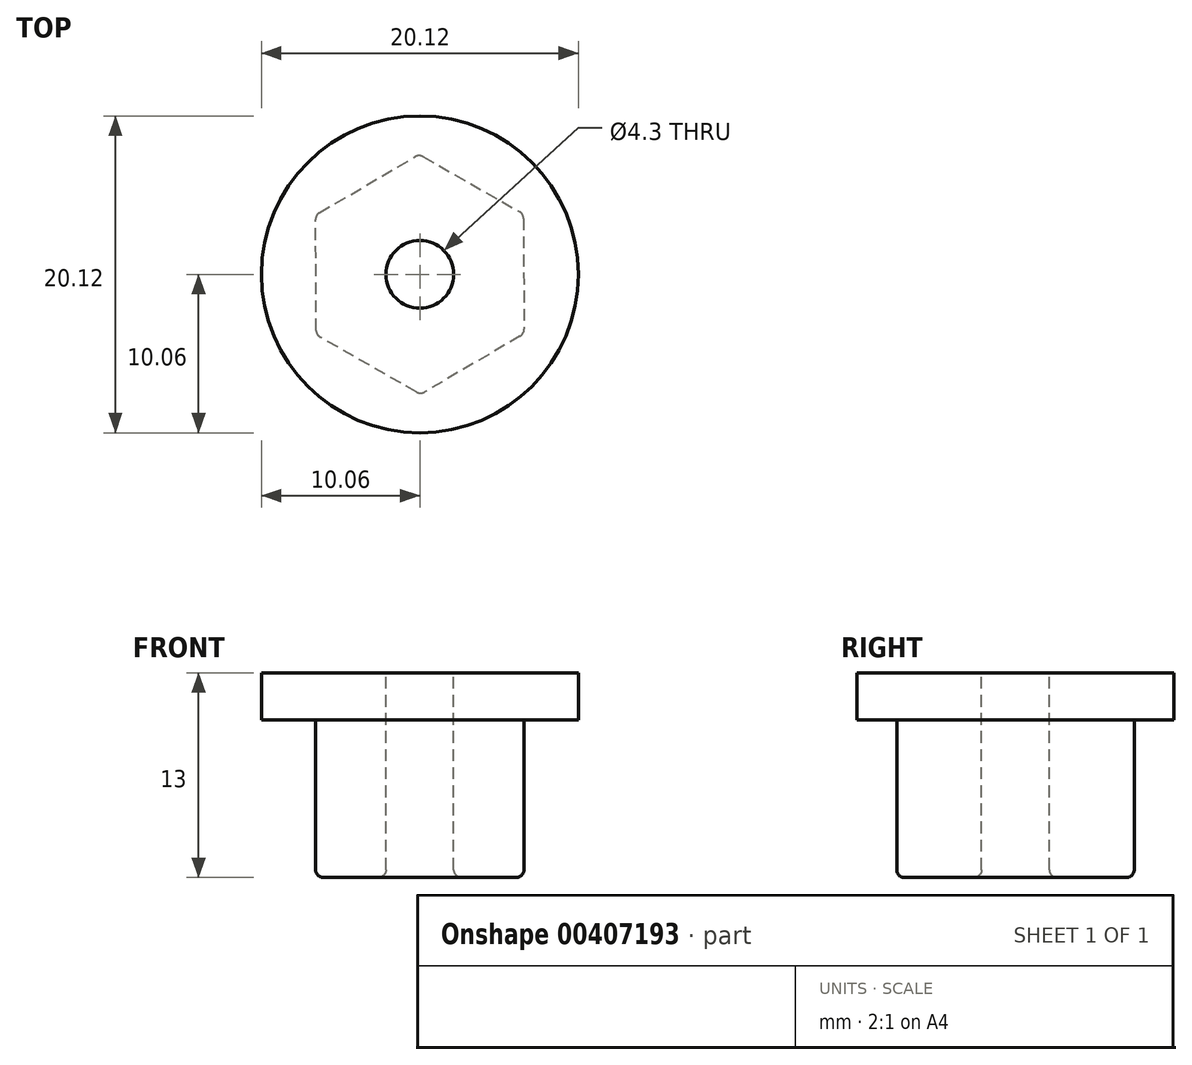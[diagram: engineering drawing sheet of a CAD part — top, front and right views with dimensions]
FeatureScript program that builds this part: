
annotation { "Feature Type Name" : "Feature", "Feature Type Description" : "" }
export const myFeature = defineFeature(function(context is Context, id is Id, definition is map)
    precondition{}
    {
        {
            var Q0;
            Q0=qCreatedBy(makeId("Top.planeOp"),FACE);
            var sketch = newSketch(context, id + "F0", { "sketchPlane" : qUnion([Q0])});
            skCircle(sketch, "E0.cCircle", {"center": v(0, 0) * mm, "radius": 6.6 * mm, "construction": true});
            skLineSegment(sketch, "E0.0", {"start": v(-0.04, 7.62) * mm, "end": v(6.58, 3.84) * mm});
            skLineSegment(sketch, "E0.1", {"start": v(6.58, 3.84) * mm, "end": v(6.62, -3.78) * mm});
            skLineSegment(sketch, "E0.2", {"start": v(6.62, -3.78) * mm, "end": v(0.04, -7.62) * mm});
            skLineSegment(sketch, "E0.3", {"start": v(0.04, -7.62) * mm, "end": v(-6.58, -3.84) * mm});
            skLineSegment(sketch, "E0.4", {"start": v(-6.58, -3.84) * mm, "end": v(-6.62, 3.78) * mm});
            skLineSegment(sketch, "E0.5", {"start": v(-6.62, 3.78) * mm, "end": v(-0.04, 7.62) * mm});
            skPoint(sketch, "E0.0.midPoint", {"position": v(3.27, 5.73) * mm});
            skSolve(sketch);
        }
        {
            var Q0;
            Q0 = qSketchRegion(id + "F0", true);
            extrude(context, id + "F1", {"entities" : qUnion([Q0]), "depth" : 10 * mm});
        }
        {
            var Q0;
            Q0=makeQuery(id+"F1.opExtrude","CAP_FACE",FACE,{"disambiguationData":[OSD([sQuery(id+"F0.wireOp",EDGE,"E0.0"),sQuery(id+"F0.wireOp",EDGE,"E0.1"),sQuery(id+"F0.wireOp",EDGE,"E0.2"),sQuery(id+"F0.wireOp",EDGE,"E0.3"),sQuery(id+"F0.wireOp",EDGE,"E0.4"),sQuery(id+"F0.wireOp",EDGE,"E0.5")])],"isStart":false});
            var sketch = newSketch(context, id + "F2", { "sketchPlane" : qUnion([Q0])});
            skCircle(sketch, "E1", {"center": v(0, 0) * mm, "radius": 10.06 * mm});
            skSolve(sketch);
        }
        {
            var Q0;
            Q0 = qSketchRegion(id + "F2", true);
            extrude(context, id + "F3", {"entities" : qUnion([Q0]), "operationType" : NewBodyOperationType.ADD, "depth" : 3 * mm});
        }
        {
            var Q0;
            Q0=makeQuery(id+"F3.opExtrude","CAP_FACE",FACE,{"disambiguationData":[OSD([sQuery(id+"F2.wireOp",EDGE,"E1")])],"isStart":false});
            var sketch = newSketch(context, id + "F4", { "sketchPlane" : qUnion([Q0])});
            skCircle(sketch, "E2", {"center": v(0, 0) * mm, "radius": 2.15 * mm});
            skSolve(sketch);
        }
        {
            var Q0;
            Q0 = qSketchRegion(id + "F4", true);
            extrude(context, id + "F5", {"entities" : qUnion([Q0]), "operationType" : NewBodyOperationType.REMOVE, "oppositeDirection" : true, "depth" : 25 * mm});
        }
        {
            var Q0;
            Q0=makeQuery(id+"F1.opExtrude","SWEPT_EDGE",EDGE,{"disambiguationData":[OSD([sQuery(id+"F0.wireOp",EDGE,"E0.0"),sQuery(id+"F0.wireOp",EDGE,"E0.5")])]});
            var Q1;
            Q1=makeQuery(id+"F1.opExtrude","SWEPT_EDGE",EDGE,{"disambiguationData":[OSD([sQuery(id+"F0.wireOp",EDGE,"E0.0"),sQuery(id+"F0.wireOp",EDGE,"E0.1")])]});
            var Q2;
            Q2=makeQuery(id+"F1.opExtrude","SWEPT_EDGE",EDGE,{"disambiguationData":[OSD([sQuery(id+"F0.wireOp",EDGE,"E0.1"),sQuery(id+"F0.wireOp",EDGE,"E0.2")])]});
            var Q3;
            Q3=makeQuery(id+"F1.opExtrude","SWEPT_EDGE",EDGE,{"disambiguationData":[OSD([sQuery(id+"F0.wireOp",EDGE,"E0.2"),sQuery(id+"F0.wireOp",EDGE,"E0.3")])]});
            var Q4;
            Q4=makeQuery(id+"F1.opExtrude","SWEPT_EDGE",EDGE,{"disambiguationData":[OSD([sQuery(id+"F0.wireOp",EDGE,"E0.3"),sQuery(id+"F0.wireOp",EDGE,"E0.4")])]});
            var Q5;
            Q5=makeQuery(id+"F1.opExtrude","SWEPT_EDGE",EDGE,{"disambiguationData":[OSD([sQuery(id+"F0.wireOp",EDGE,"E0.4"),sQuery(id+"F0.wireOp",EDGE,"E0.5")])]});
            var Q6;
            Q6=makeQuery(id+"F1.opExtrude","CAP_EDGE",EDGE,{"disambiguationData":[OSD([sQuery(id+"F0.wireOp",EDGE,"E0.5")])],"isStart":true});
            var Q7;
            Q7=makeQuery(id+"F1.opExtrude","CAP_EDGE",EDGE,{"disambiguationData":[OSD([sQuery(id+"F0.wireOp",EDGE,"E0.4")])],"isStart":true});
            var Q8;
            Q8=makeQuery(id+"F1.opExtrude","CAP_EDGE",EDGE,{"disambiguationData":[OSD([sQuery(id+"F0.wireOp",EDGE,"E0.3")])],"isStart":true});
            var Q9;
            Q9=makeQuery(id+"F1.opExtrude","CAP_EDGE",EDGE,{"disambiguationData":[OSD([sQuery(id+"F0.wireOp",EDGE,"E0.2")])],"isStart":true});
            var Q10;
            Q10=makeQuery(id+"F1.opExtrude","CAP_EDGE",EDGE,{"disambiguationData":[OSD([sQuery(id+"F0.wireOp",EDGE,"E0.1")])],"isStart":true});
            var Q11;
            Q11=makeQuery(id+"F1.opExtrude","CAP_EDGE",EDGE,{"disambiguationData":[OSD([sQuery(id+"F0.wireOp",EDGE,"E0.0")])],"isStart":true});
            var Q12;
            Q12=makeQuery(id+"F5.boolean.opBoolean","INTERSECT",EDGE,{"derivedFrom":[makeQuery(id+"F1.opExtrude","CAP_FACE",FACE,{"disambiguationData":[OSD([sQuery(id+"F0.wireOp",EDGE,"E0.0"),sQuery(id+"F0.wireOp",EDGE,"E0.1"),sQuery(id+"F0.wireOp",EDGE,"E0.2"),sQuery(id+"F0.wireOp",EDGE,"E0.3"),sQuery(id+"F0.wireOp",EDGE,"E0.4"),sQuery(id+"F0.wireOp",EDGE,"E0.5")])],"isStart":true}),makeQuery(id+"F5.opExtrude","SWEPT_FACE",FACE,{"disambiguationData":[OSD([sQuery(id+"F4.wireOp",EDGE,"E2")])]})]});
            fillet(context, id + "F6", {"entities" : qUnion([Q0, Q1, Q2, Q3, Q4, Q5, Q6, Q7, Q8, Q9, Q10, Q11, Q12]), "radius" : 0.5 * mm, "tangentPropagation" : true, "allowEdgeOverflow" : false});
        }
    });
